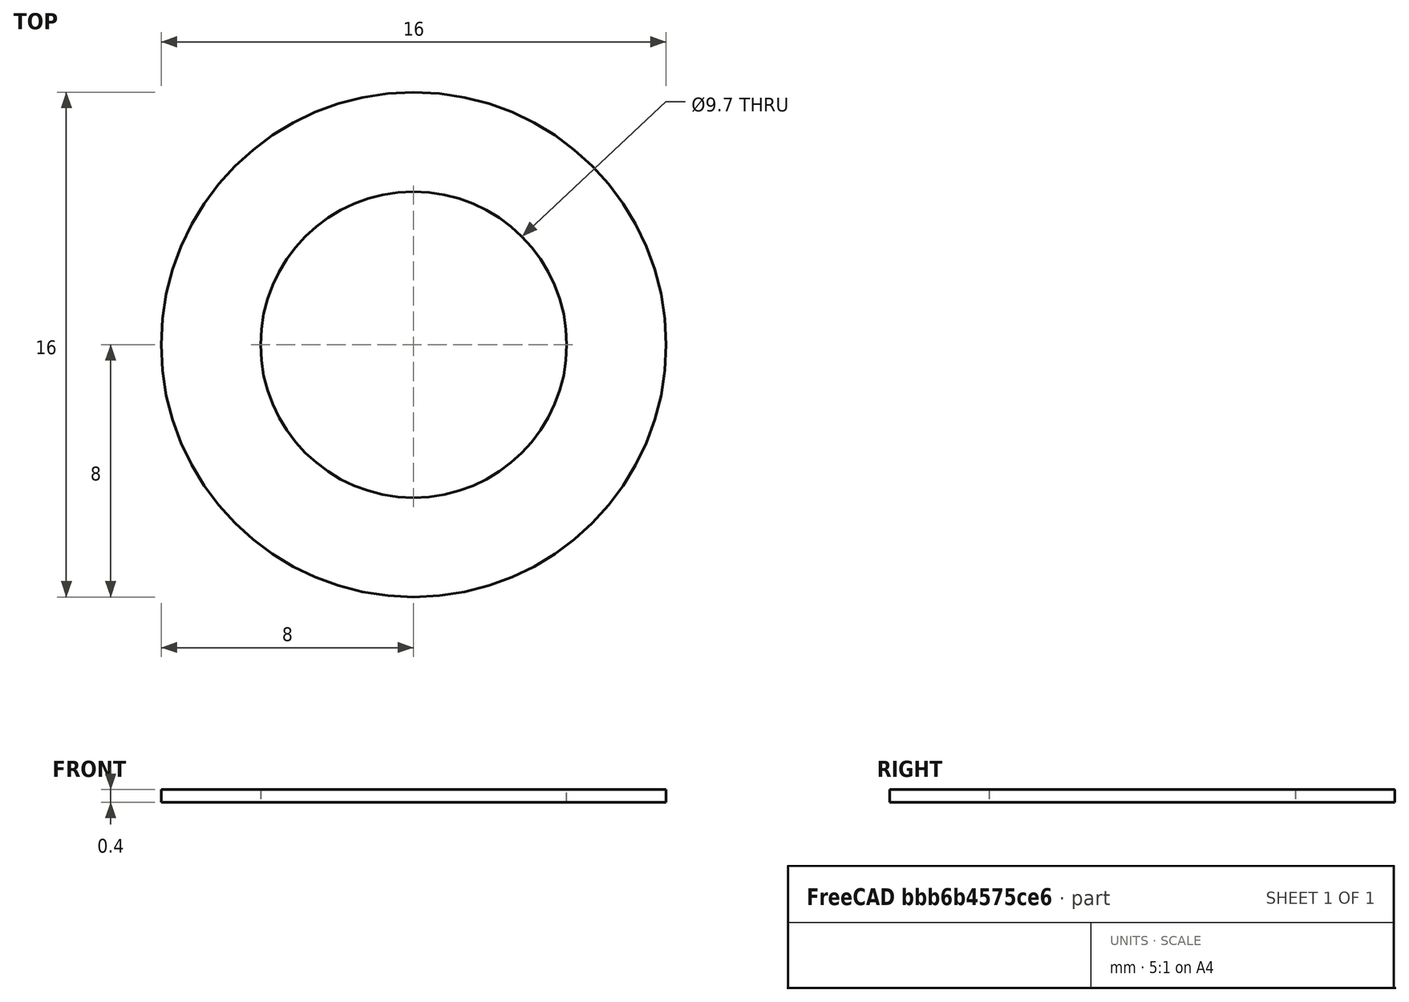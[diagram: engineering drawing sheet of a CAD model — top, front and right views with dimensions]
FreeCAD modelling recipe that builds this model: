
FCSTD DOCUMENT  (FreeCAD 0.19R16945 (Git))
Label: Washer_M9.7x0.4mm
License: All rights reserved
LicenseURL: http://en.wikipedia.org/wiki/All_rights_reserved
objects: Sketcher::SketchObject×1, PartDesign::Pad×1, PartDesign::Body×1
note: 4 computed .brp shape members not serialized (recipe doc carries the construction recipe); baked Part::Feature solids carry a one-line shape summary decoded from their .brp

FEATURE [Sketcher::SketchObject] Sketch
  MapMode = 5
  Support = -> [XY_Plane]
  sketch-geometry (2):
    g0: Circle CenterX=0 CenterY=0 CenterZ=0 NormalX=0 NormalY=0 NormalZ=1 AngleXU=0 Radius=4.85
    g1: Circle CenterX=0 CenterY=0 CenterZ=0 NormalX=0 NormalY=0 NormalZ=1 AngleXU=0 Radius=8
  constraints (4):
    c: Coincident(g0,g-1)
    c: Coincident(g1,g0)
    c: Radius(g0) = 4.85
    c: Radius(g1) = 8
FEATURE [PartDesign::Pad] Pad
  Length = 0.4
  Length2 = 100
  Profile = -> Sketch
  Type = 0
FEATURE [PartDesign::Body] Body
  Group = -> [Sketch,Pad]
  Origin = -> Origin
  Tip = -> Pad
